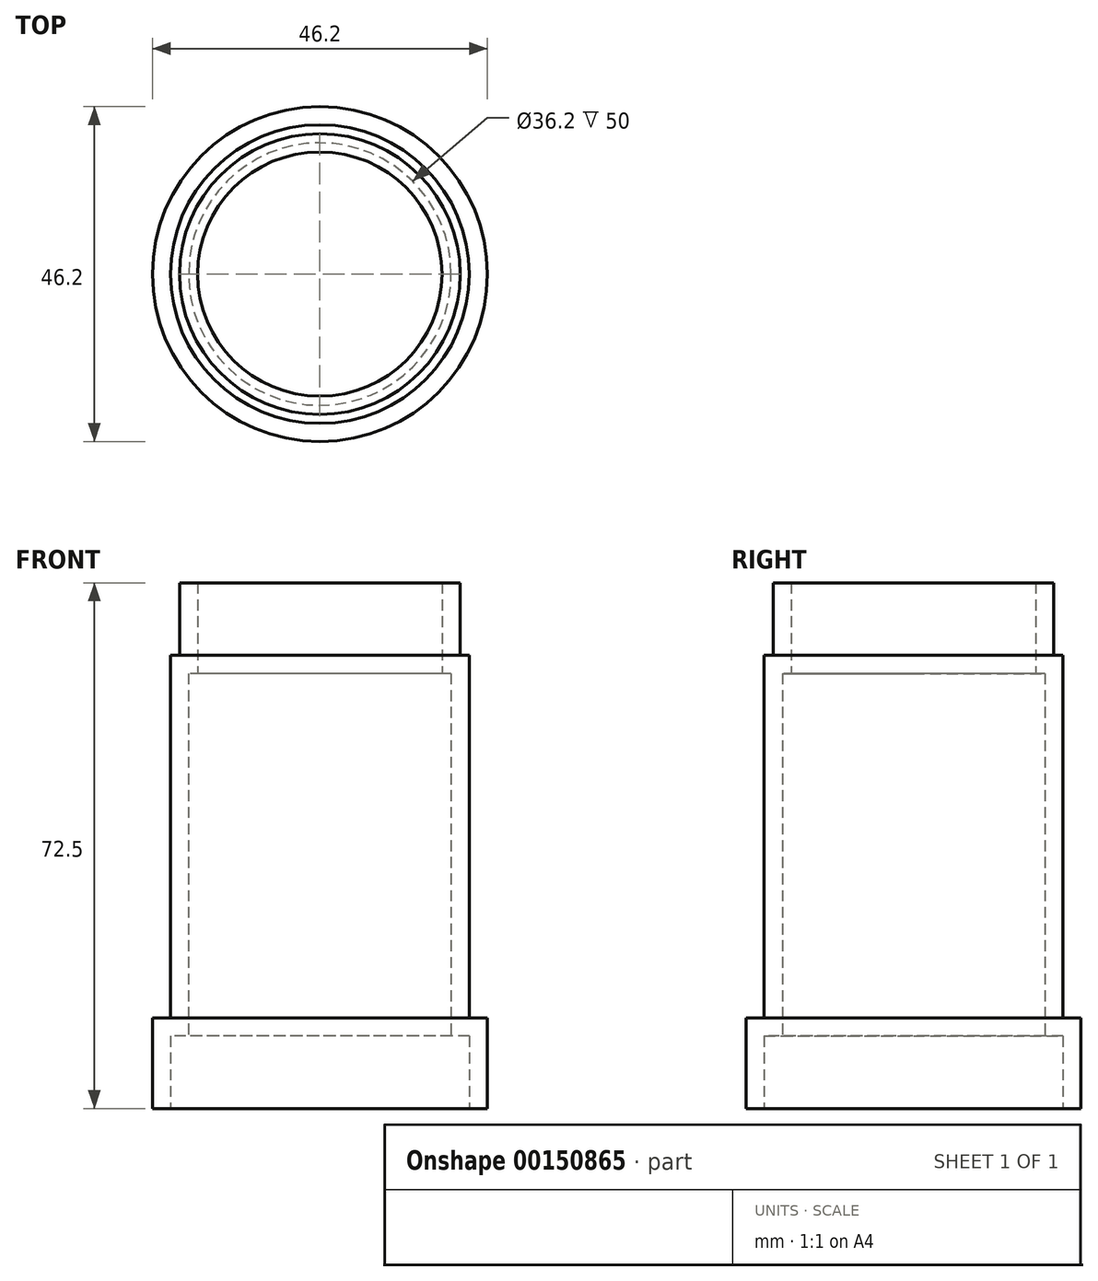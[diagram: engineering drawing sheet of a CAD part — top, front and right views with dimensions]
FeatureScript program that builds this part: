
annotation { "Feature Type Name" : "Feature", "Feature Type Description" : "" }
export const myFeature = defineFeature(function(context is Context, id is Id, definition is map)
    precondition{}
    {
        {
            var Q0;
            Q0=qCreatedBy(makeId("Top.planeOp"),FACE);
            var sketch = newSketch(context, id + "F0", { "sketchPlane" : qUnion([Q0])});
            skCircle(sketch, "E0", {"center": v(0, 0) * mm, "radius": 23.1 * mm});
            skSolve(sketch);
        }
        {
            var Q0;
            Q0=makeQuery(id+"F0.imprint","IMPRINT",FACE,{"disambiguationData":[TD([[makeQuery(id+"F0.imprint","IMPRINT",EDGE,{"derivedFrom":sQuery(id+"F0.wireOp",EDGE,"E0")}),1.0]])]});
            extrude(context, id + "F1", {"entities" : qUnion([Q0]), "depth" : 12.5 * mm});
        }
        {
            var Q0;
            Q0=makeQuery(id+"F1.opExtrude","CAP_FACE",FACE,{"disambiguationData":[OSD([sQuery(id+"F0.wireOp",EDGE,"E0")])],"isStart":false});
            var sketch = newSketch(context, id + "F2", { "sketchPlane" : qUnion([Q0])});
            skCircle(sketch, "E1", {"center": v(0, 0) * mm, "radius": 20.6 * mm});
            skSolve(sketch);
        }
        {
            var Q0;
            Q0=makeQuery(id+"F2.imprint","IMPRINT",FACE,{"disambiguationData":[TD([[makeQuery(id+"F2.imprint","IMPRINT",EDGE,{"derivedFrom":sQuery(id+"F2.wireOp",EDGE,"E1")}),1.0]])]});
            extrude(context, id + "F3", {"entities" : qUnion([Q0]), "operationType" : NewBodyOperationType.ADD, "depth" : 50 * mm});
        }
        {
            var Q0;
            Q0=makeQuery(id+"F3.opExtrude","CAP_FACE",FACE,{"disambiguationData":[OSD([sQuery(id+"F2.wireOp",EDGE,"E1")])],"isStart":false});
            var sketch = newSketch(context, id + "F4", { "sketchPlane" : qUnion([Q0])});
            skCircle(sketch, "E2", {"center": v(0, 0) * mm, "radius": 19.35 * mm});
            skSolve(sketch);
        }
        {
            var Q0;
            Q0=makeQuery(id+"F4.imprint","IMPRINT",FACE,{"disambiguationData":[TD([[makeQuery(id+"F4.imprint","IMPRINT",EDGE,{"derivedFrom":sQuery(id+"F4.wireOp",EDGE,"E2")}),1.0]])]});
            extrude(context, id + "F5", {"entities" : qUnion([Q0]), "operationType" : NewBodyOperationType.ADD, "depth" : 10 * mm});
        }
        {
            var Q0;
            Q0=makeQuery(id+"F5.opExtrude","CAP_FACE",FACE,{"disambiguationData":[OSD([sQuery(id+"F4.wireOp",EDGE,"E2")])],"isStart":false});
            var Q1;
            Q1=makeQuery(id+"F1.opExtrude","CAP_FACE",FACE,{"disambiguationData":[OSD([sQuery(id+"F0.wireOp",EDGE,"E0")])],"isStart":true});
            shell(context, id + "F6", {"entities" : qUnion([Q0, Q1]), "thickness" : 2.5 * mm});
        }
    });
